# Revit family: Faucet-Valve_Trim-KOHLER-Toobi-K-T8979-4
name_source: partatom
category: Generic Models
revit_build: Autodesk Revit 2015 (Build: 20140606_1530(x64)
units: mm (PartAtom-declared; Revit-internal decimal feet)

## types (2) — shared parameters
ADA Compliant = Yes
Assembly Code = C1030200
Date Modified = 10/05/2017
Default Elevation = 42"
Description = Toobi Rite-Temp valve trim with diverter, valve not included
Height = 6 1/2"
Inlet Connector = Inlet Connection
Length = 4 1/2"
Manufacturer = KOHLER Co.
MasterFormat 1995 = 10820
MasterFormat 2004 = 10.28.13
Material = Premium Metal Construction
Outlet Connector = Outlet Connection
Product Documentation Link = http://www.us.kohler.com
Product Name = Toobi
Product Page URL = http://www.us.kohler.com
URL = http://www.us.kohler.com
Width = 6 1/2"

## per-type parameters (varying)
| type | Finish | Model | Type |
| CP-Polished Chrome | Kohler-Metal-CP-Polished_Chrome | K-T8979-4-CP | 1 |
| BN-Vibrant Brushed Nickel | Kohler-Metal-BN-Vibrant_Brushed_Nickel | K-T8979-4-BN | 2 |

## geometry (parser evidence)
native form markers: Sweep x6
no freeform markers — native parametric forms only
